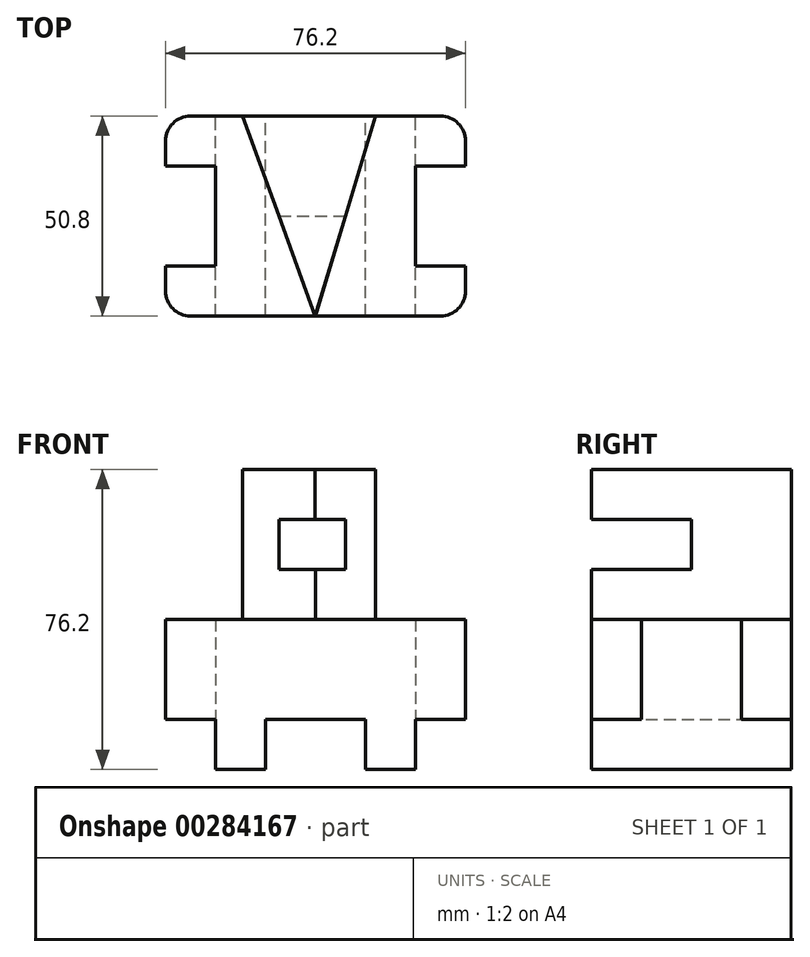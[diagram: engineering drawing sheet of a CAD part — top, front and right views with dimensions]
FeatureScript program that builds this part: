
annotation { "Feature Type Name" : "Feature", "Feature Type Description" : "" }
export const myFeature = defineFeature(function(context is Context, id is Id, definition is map)
    precondition{}
    {
        {
            var Q0;
            Q0=qCreatedBy(makeId("Top.planeOp"),FACE);
            var sketch = newSketch(context, id + "F0", { "sketchPlane" : qUnion([Q0])});
            skLineSegment(sketch, "E0.bottom", {"start": v(6.35, 0) * mm, "end": v(69.85, 0) * mm});
            skLineSegment(sketch, "E0.top", {"start": v(6.35, 50.8) * mm, "end": v(69.85, 50.8) * mm});
            skLineSegment(sketch, "E0.left", {"start": v(0, 6.35) * mm, "end": v(0, 12.7) * mm});
            skLineSegment(sketch, "E0.right", {"start": v(76.2, 6.35) * mm, "end": v(76.2, 12.7) * mm});
            skLineSegment(sketch, "E1.top", {"start": v(76.2, 38.1) * mm, "end": v(63.5, 38.1) * mm});
            skLineSegment(sketch, "E1.right", {"start": v(63.5, 25.4) * mm, "end": v(63.5, 38.1) * mm});
            skLineSegment(sketch, "E2.top", {"start": v(63.5, 12.7) * mm, "end": v(76.2, 12.7) * mm});
            skLineSegment(sketch, "E2.left", {"start": v(63.5, 25.4) * mm, "end": v(63.5, 12.7) * mm});
            skPoint(sketch, "E1.left.start.orphan", {"position": v(76.2, 25.4) * mm});
            skLineSegment(sketch, "E3.trimOffspring", {"start": v(76.2, 38.1) * mm, "end": v(76.2, 44.45) * mm});
            skLineSegment(sketch, "E4.MirrorCS", {"start": v(12.7, 12.7) * mm, "end": v(0, 12.7) * mm});
            skLineSegment(sketch, "E5.MirrorCS", {"start": v(12.7, 25.4) * mm, "end": v(12.7, 12.7) * mm});
            skLineSegment(sketch, "E6.MirrorCS", {"start": v(0, 38.1) * mm, "end": v(12.7, 38.1) * mm});
            skLineSegment(sketch, "E7.MirrorCS", {"start": v(12.7, 25.4) * mm, "end": v(12.7, 38.1) * mm});
            skLineSegment(sketch, "E8.trimOffspring", {"start": v(0, 38.1) * mm, "end": v(0, 44.45) * mm});
            skPoint(sketch, "E9.visualSharp", {"position": v(0, 50.8) * mm});
            skArc(sketch, "E9.filletArc", {"start": v(6.35, 50.8) * mm, "mid": v(1.86, 48.94) * mm, "end": v(0, 44.45) * mm});
            skPoint(sketch, "E10.visualSharp", {"position": v(0, 0) * mm});
            skArc(sketch, "E10.filletArc", {"start": v(0, 6.35) * mm, "mid": v(1.86, 1.86) * mm, "end": v(6.35, 0) * mm});
            skPoint(sketch, "E11.visualSharp", {"position": v(76.2, 0) * mm});
            skArc(sketch, "E11.filletArc", {"start": v(69.85, 0) * mm, "mid": v(74.34, 1.86) * mm, "end": v(76.2, 6.35) * mm});
            skPoint(sketch, "E12.visualSharp", {"position": v(76.2, 50.8) * mm});
            skArc(sketch, "E12.filletArc", {"start": v(76.2, 44.45) * mm, "mid": v(74.34, 48.94) * mm, "end": v(69.85, 50.8) * mm});
            skSolve(sketch);
        }
        {
            var Q0;
            Q0=makeQuery(id+"F0.imprint","IMPRINT",FACE,{"disambiguationData":[TD([[makeQuery(id+"F0.imprint","IMPRINT",EDGE,{"derivedFrom":sQuery(id+"F0.wireOp",EDGE,"E0.bottom")}),1.0]])]});
            extrude(context, id + "F1", {"entities" : qUnion([Q0]), "depth" : 25.4 * mm});
        }
        {
            var Q0;
            Q0=makeQuery(id+"F1.opExtrude","CAP_FACE",FACE,{"disambiguationData":[OSD([sQuery(id+"F0.wireOp",EDGE,"E0.bottom"),sQuery(id+"F0.wireOp",EDGE,"E0.top"),sQuery(id+"F0.wireOp",EDGE,"E0.left"),sQuery(id+"F0.wireOp",EDGE,"E0.right"),sQuery(id+"F0.wireOp",EDGE,"E1.top"),sQuery(id+"F0.wireOp",EDGE,"E1.right"),sQuery(id+"F0.wireOp",EDGE,"E2.top"),sQuery(id+"F0.wireOp",EDGE,"E2.left"),sQuery(id+"F0.wireOp",EDGE,"E3.trimOffspring"),sQuery(id+"F0.wireOp",EDGE,"E4.MirrorCS"),sQuery(id+"F0.wireOp",EDGE,"E5.MirrorCS"),sQuery(id+"F0.wireOp",EDGE,"E6.MirrorCS"),sQuery(id+"F0.wireOp",EDGE,"E7.MirrorCS"),sQuery(id+"F0.wireOp",EDGE,"E8.trimOffspring"),sQuery(id+"F0.wireOp",EDGE,"E9.filletArc"),sQuery(id+"F0.wireOp",EDGE,"E10.filletArc"),sQuery(id+"F0.wireOp",EDGE,"E11.filletArc"),sQuery(id+"F0.wireOp",EDGE,"E12.filletArc")])],"isStart":true});
            var sketch = newSketch(context, id + "F2", { "sketchPlane" : qUnion([Q0])});
            skLineSegment(sketch, "E13.bottom", {"start": v(63.5, 0) * mm, "end": v(50.81, 0) * mm});
            skLineSegment(sketch, "E13.top", {"start": v(63.5, -50.8) * mm, "end": v(50.81, -50.8) * mm});
            skLineSegment(sketch, "E13.left", {"start": v(63.5, 0) * mm, "end": v(63.5, -50.8) * mm});
            skLineSegment(sketch, "E13.right", {"start": v(50.81, 0) * mm, "end": v(50.81, -50.8) * mm});
            skLineSegment(sketch, "E14.bottom", {"start": v(12.7, 0) * mm, "end": v(25.4, 0) * mm});
            skLineSegment(sketch, "E14.top", {"start": v(12.7, -50.8) * mm, "end": v(25.4, -50.8) * mm});
            skLineSegment(sketch, "E14.left", {"start": v(12.7, 0) * mm, "end": v(12.7, -50.8) * mm});
            skLineSegment(sketch, "E14.right", {"start": v(25.4, 0) * mm, "end": v(25.4, -50.8) * mm});
            skSolve(sketch);
        }
        {
            var Q0;
            {var subQ3=sQuery(id+"F2.wireOp",EDGE,"E13.bottom");Q0=makeQuery(id+"F2.imprint","IMPRINT",FACE,{"disambiguationData":[TD([[makeQuery(id+"F2.imprint","IMPRINT",EDGE,{"derivedFrom":subQ3}),-1.0]])]});}
            var Q1;
            {var subQ3=sQuery(id+"F2.wireOp",EDGE,"E14.bottom");Q1=makeQuery(id+"F2.imprint","IMPRINT",FACE,{"disambiguationData":[TD([[makeQuery(id+"F2.imprint","IMPRINT",EDGE,{"derivedFrom":subQ3}),-1.0]])]});}
            extrude(context, id + "F3", {"entities" : qUnion([Q0, Q1]), "operationType" : NewBodyOperationType.ADD, "depth" : 12.7 * mm});
        }
        {
            var Q0;
            Q0=makeQuery(id+"F1.opExtrude","CAP_FACE",FACE,{"disambiguationData":[OSD([sQuery(id+"F0.wireOp",EDGE,"E0.bottom"),sQuery(id+"F0.wireOp",EDGE,"E0.top"),sQuery(id+"F0.wireOp",EDGE,"E0.left"),sQuery(id+"F0.wireOp",EDGE,"E0.right"),sQuery(id+"F0.wireOp",EDGE,"E1.top"),sQuery(id+"F0.wireOp",EDGE,"E1.right"),sQuery(id+"F0.wireOp",EDGE,"E2.top"),sQuery(id+"F0.wireOp",EDGE,"E2.left"),sQuery(id+"F0.wireOp",EDGE,"E3.trimOffspring"),sQuery(id+"F0.wireOp",EDGE,"E4.MirrorCS"),sQuery(id+"F0.wireOp",EDGE,"E5.MirrorCS"),sQuery(id+"F0.wireOp",EDGE,"E6.MirrorCS"),sQuery(id+"F0.wireOp",EDGE,"E7.MirrorCS"),sQuery(id+"F0.wireOp",EDGE,"E8.trimOffspring"),sQuery(id+"F0.wireOp",EDGE,"E9.filletArc"),sQuery(id+"F0.wireOp",EDGE,"E10.filletArc"),sQuery(id+"F0.wireOp",EDGE,"E11.filletArc"),sQuery(id+"F0.wireOp",EDGE,"E12.filletArc")])],"isStart":false});
            var sketch = newSketch(context, id + "F4", { "sketchPlane" : qUnion([Q0])});
            skLineSegment(sketch, "E15", {"start": v(38.1, 0) * mm, "end": v(53.28, 50.8) * mm});
            skLineSegment(sketch, "E16", {"start": v(38.1, 0) * mm, "end": v(19.53, 50.8) * mm});
            skLineSegment(sketch, "E17", {"start": v(19.53, 50.8) * mm, "end": v(53.28, 50.8) * mm});
            skSolve(sketch);
        }
        {
            var Q0;
            Q0=makeQuery(id+"F4.imprint","IMPRINT",FACE,{"disambiguationData":[TD([[makeQuery(id+"F4.imprint","IMPRINT",EDGE,{"derivedFrom":sQuery(id+"F4.wireOp",EDGE,"E15")}),1.0]])]});
            extrude(context, id + "F5", {"entities" : qUnion([Q0]), "operationType" : NewBodyOperationType.ADD, "depth" : 12.7 * mm});
        }
        {
            var Q0;
            Q0=makeQuery(id+"F5.opExtrude","CAP_FACE",FACE,{"disambiguationData":[OSD([sQuery(id+"F4.wireOp",EDGE,"E15"),sQuery(id+"F4.wireOp",EDGE,"E16"),sQuery(id+"F4.wireOp",EDGE,"E17")])],"isStart":false});
            var sketch = newSketch(context, id + "F6", { "sketchPlane" : qUnion([Q0])});
            skLineSegment(sketch, "E18", {"start": v(28.81, 25.4) * mm, "end": v(45.69, 25.4) * mm});
            skSolve(sketch);
        }
        {
            var Q0;
            {var subQ0=sQuery(id+"F6.wireOp",EDGE,"E18");Q0=makeQuery(id+"F6.imprint","IMPRINT",FACE,{"disambiguationData":[TD([[makeQuery(id+"F6.imprint","IMPRINT",EDGE,{"derivedFrom":subQ0}),1.0]])]});}
            extrude(context, id + "F7", {"entities" : qUnion([Q0]), "operationType" : NewBodyOperationType.ADD, "depth" : 12.7 * mm});
        }
        {
            var Q0;
            Q0=makeQuery(id+"F7.opExtrude","CAP_FACE",FACE,{"disambiguationData":[OSD([sQuery(id+"F4.wireOp",EDGE,"E15"),sQuery(id+"F4.wireOp",EDGE,"E16"),sQuery(id+"F4.wireOp",EDGE,"E17"),sQuery(id+"F6.wireOp",EDGE,"E18")])],"isStart":false});
            var sketch = newSketch(context, id + "F8", { "sketchPlane" : qUnion([Q0])});
            skLineSegment(sketch, "E19", {"start": v(28.81, 25.4) * mm, "end": v(37.92, 0) * mm});
            skLineSegment(sketch, "E20", {"start": v(37.92, 0) * mm, "end": v(45.69, 25.4) * mm});
            skSolve(sketch);
        }
        {
            var Q0;
            Q0=makeQuery(id+"F8.imprint","IMPRINT",FACE,{"disambiguationData":[TD([[makeQuery(id+"F8.imprint","IMPRINT",EDGE,{"derivedFrom":sQuery(id+"F8.wireOp",EDGE,"E19")}),1.0]])]});
            extrude(context, id + "F9", {"entities" : qUnion([Q0]), "depth" : 12.7 * mm});
        }
        {
            var Q0;
            Q0=makeQuery(id+"F7.opExtrude","CAP_FACE",FACE,{"disambiguationData":[OSD([sQuery(id+"F4.wireOp",EDGE,"E15"),sQuery(id+"F4.wireOp",EDGE,"E16"),sQuery(id+"F4.wireOp",EDGE,"E17"),sQuery(id+"F6.wireOp",EDGE,"E18")])],"isStart":false});
            extrude(context, id + "F10", {"entities" : qUnion([Q0]), "operationType" : NewBodyOperationType.ADD, "depth" : 12.7 * mm});
        }
    });
